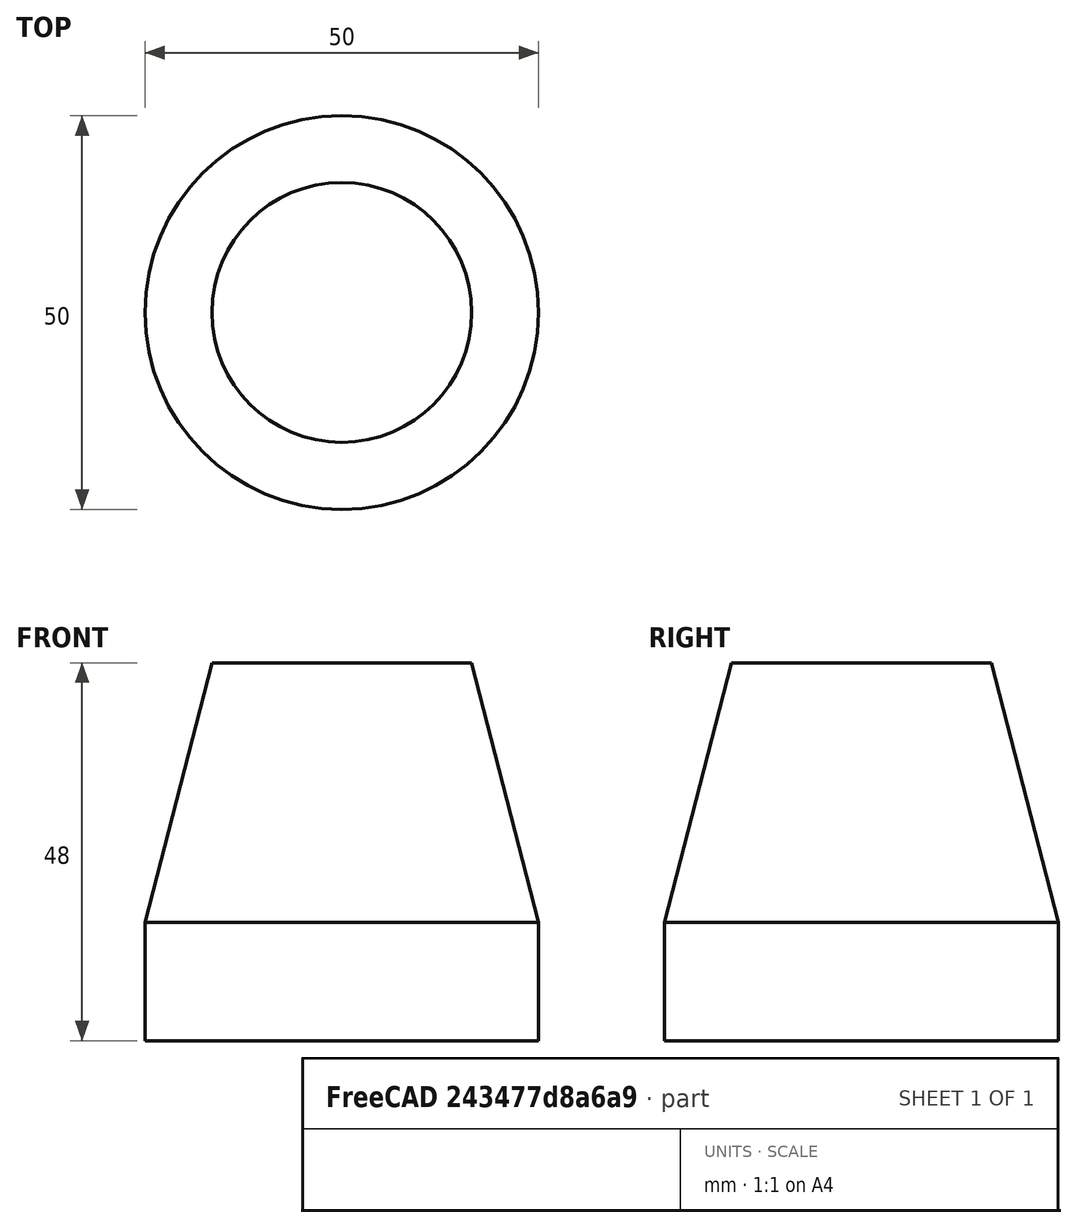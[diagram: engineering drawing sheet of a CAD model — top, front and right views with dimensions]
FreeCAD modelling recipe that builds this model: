
FCSTD DOCUMENT  (FreeCAD 0.19R24291 (Git))
Label: antenna
License: All rights reserved
LicenseURL: http://en.wikipedia.org/wiki/All_rights_reserved
objects: Sketcher::SketchObject×1, PartDesign::Revolution×1, PartDesign::Body×1
note: 4 computed .brp shape members not serialized (recipe doc carries the construction recipe); baked Part::Feature solids carry a one-line shape summary decoded from their .brp

FEATURE [Sketcher::SketchObject] Sketch
  FullyConstrained = true
  MapMode = 5
  Placement = pos=(0,0,0) rot=(1,0,0;1.5708rad)
  Support = -> [XZ_Plane]
  sketch-geometry (5):
    g0: LineSegment StartX=0 StartY=0 StartZ=0 EndX=-25 EndY=0 EndZ=0
    g1: LineSegment StartX=-25 StartY=0 StartZ=0 EndX=-25 EndY=15 EndZ=0
    g2: LineSegment StartX=0 StartY=48 StartZ=0 EndX=-16.5 EndY=48 EndZ=0
    g3: LineSegment StartX=-16.5 StartY=48 StartZ=0 EndX=-25 EndY=15 EndZ=0
    g4: LineSegment StartX=0 StartY=48 StartZ=0 EndX=0 EndY=0 EndZ=0
  constraints (14):
    c: Coincident(g0,g-1)
    c: Horizontal(g0)
    c: Coincident(g1,g0)
    c: Vertical(g1)
    c: DistanceX(g0,g0) = 25
    c: DistanceY(g1,g1) = 15
    c: PointOnObject(g2,g-2)
    c: Horizontal(g2)
    c: Distance(g2,g0) = 48
    c: Coincident(g3,g2)
    c: Coincident(g3,g1)
    c: DistanceX(g2,g2) = 16.5
    c: Coincident(g4,g2)
    c: Coincident(g4,g0)
FEATURE [PartDesign::Revolution] Revolution
  Angle = 360
  Axis = (0,-2e-16,1)
  Base = (0,0,0)
  Placement = pos=(0,0,0) rot=(1,0,0;1.5708rad)
  Profile = -> Sketch
  ReferenceAxis = -> Sketch [V_Axis]
FEATURE [PartDesign::Body] Body
  Group = -> [Sketch,Revolution]
  Origin = -> Origin
  Tip = -> Revolution
